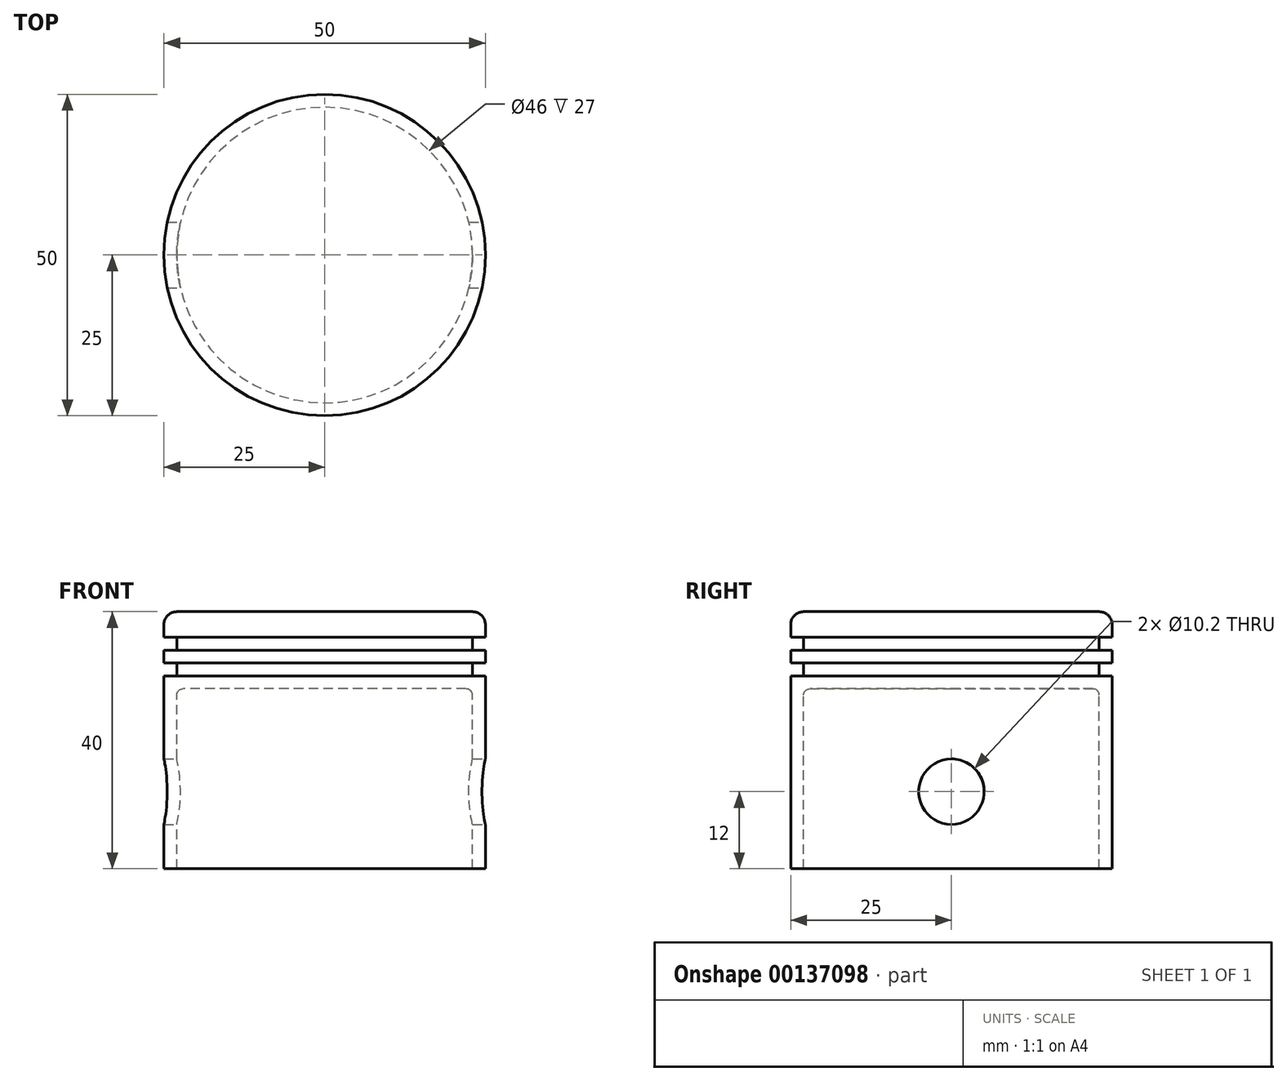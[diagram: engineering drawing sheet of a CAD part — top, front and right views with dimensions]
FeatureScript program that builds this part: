
annotation { "Feature Type Name" : "Feature", "Feature Type Description" : "" }
export const myFeature = defineFeature(function(context is Context, id is Id, definition is map)
    precondition{}
    {
        {
            var Q0;
            Q0=qCreatedBy(makeId("Right.planeOp"),FACE);
            var sketch = newSketch(context, id + "F0", { "sketchPlane" : qUnion([Q0])});
            skLineSegment(sketch, "E0.bottom", {"start": v(0, 20) * mm, "end": v(25, 20) * mm});
            skLineSegment(sketch, "E0.top", {"start": v(0, -20) * mm, "end": v(25, -20) * mm});
            skLineSegment(sketch, "E0.left", {"start": v(0, 20) * mm, "end": v(0, -20) * mm});
            skLineSegment(sketch, "E0.right", {"start": v(25, 20) * mm, "end": v(25, -20) * mm});
            skLineSegment(sketch, "E1.bottom", {"start": v(25, 16) * mm, "end": v(23, 16) * mm});
            skLineSegment(sketch, "E1.top", {"start": v(25, 14) * mm, "end": v(23, 14) * mm});
            skLineSegment(sketch, "E1.left", {"start": v(25, 16) * mm, "end": v(25, 14) * mm});
            skLineSegment(sketch, "E1.right", {"start": v(23, 16) * mm, "end": v(23, 14) * mm});
            skLineSegment(sketch, "E2.0.1.0", {"start": v(0, 16) * mm, "end": v(0, -24) * mm});
            skLineSegment(sketch, "E2.0.1.1", {"start": v(23, 12) * mm, "end": v(23, 10) * mm});
            skLineSegment(sketch, "E2.0.1.2", {"start": v(25, 10) * mm, "end": v(23, 10) * mm});
            skLineSegment(sketch, "E2.0.1.3", {"start": v(25, 12) * mm, "end": v(23, 12) * mm});
            skLineSegment(sketch, "E2.0.1.4", {"start": v(25, 12) * mm, "end": v(25, 10) * mm});
            skLineSegment(sketch, "E2.direction1", {"start": v(0, -20) * mm, "end": v(25, -20) * mm, "construction": true});
            skLineSegment(sketch, "E2.direction2", {"start": v(0, -20) * mm, "end": v(0, -24) * mm, "construction": true});
            skSolve(sketch);
        }
        {
            var Q0;
            {var subQ1=sQuery(id+"F0.wireOp",EDGE,"E0.bottom");Q0=makeQuery(id+"F0.imprint","IMPRINT",FACE,{"disambiguationData":[TD([[makeQuery(id+"F0.imprint","IMPRINT",EDGE,{"derivedFrom":subQ1}),-1.0]])]});}
            var Q1;
            Q1=sQuery(id+"F0.wireOp",EDGE,"E2.0.1.0");
            revolve(context, id + "F1", {"entities" : qUnion([Q0]), "axis" : qUnion([Q1]), "revolveType" : RevolveType.FULL});
        }
        {
            var Q0;
            Q0=makeQuery(id+"F1.opRevolve","SWEPT_EDGE",EDGE,{"disambiguationData":[OSD([sQuery(id+"F0.wireOp",EDGE,"E0.bottom"),sQuery(id+"F0.wireOp",EDGE,"E0.right")])]});
            fillet(context, id + "F2", {"entities" : qUnion([Q0]), "radius" : 2 * mm, "tangentPropagation" : true, "allowEdgeOverflow" : false});
        }
        {
            var Q0;
            Q0=qCreatedBy(makeId("Right.planeOp"),FACE);
            var sketch = newSketch(context, id + "F3", { "sketchPlane" : qUnion([Q0])});
            skLineSegment(sketch, "E3", {"start": v(0, -20) * mm, "end": v(0, 8) * mm});
            skLineSegment(sketch, "E4", {"start": v(0, 8) * mm, "end": v(22, 8) * mm});
            skLineSegment(sketch, "E5", {"start": v(23, 7) * mm, "end": v(23, -20) * mm});
            skLineSegment(sketch, "E6.0", {"start": v(-25, 10) * mm, "end": v(25, 10) * mm});
            skLineSegment(sketch, "E7.0", {"start": v(-25, 12) * mm, "end": v(25, 12) * mm});
            skLineSegment(sketch, "E7.1", {"start": v(-25, 14) * mm, "end": v(25, 14) * mm});
            skLineSegment(sketch, "E7.2", {"start": v(-25, 16) * mm, "end": v(25, 16) * mm});
            skLineSegment(sketch, "E7.3", {"start": v(25, 18) * mm, "end": v(-25, 18) * mm});
            skPoint(sketch, "E8.visualSharp", {"position": v(23, 8) * mm});
            skArc(sketch, "E8.filletArc", {"start": v(23, 7) * mm, "mid": v(22.7, 7.7) * mm, "end": v(22, 8) * mm});
            skLineSegment(sketch, "E9", {"start": v(0, -20) * mm, "end": v(23, -20) * mm});
            skPoint(sketch, "E10.orphan", {"position": v(-25, -20) * mm});
            skPoint(sketch, "E11.orphan", {"position": v(25, -20) * mm});
            skSolve(sketch);
        }
        {
            var Q0;
            Q0=makeQuery(id+"F3.imprint","IMPRINT",FACE,{"disambiguationData":[TD([[makeQuery(id+"F3.imprint","IMPRINT",EDGE,{"derivedFrom":sQuery(id+"F3.wireOp",EDGE,"E3")}),-1.0]])]});
            var Q1;
            Q1=sQuery(id+"F3.wireOp",EDGE,"E3");
            revolve(context, id + "F4", {"operationType" : NewBodyOperationType.REMOVE, "entities" : qUnion([Q0]), "axis" : qUnion([Q1]), "revolveType" : RevolveType.FULL, "oppositeDirection" : true});
        }
        {
            var Q0;
            Q0=qCreatedBy(makeId("Right.planeOp"),FACE);
            cPlane(context, id + "F5", {"entities" : qUnion([Q0]), "cplaneType" : CPlaneType.OFFSET, "offset" : 25 * mm, "width" : 150 * mm, "height" : 150 * mm});
        }
        {
            var Q0;
            Q0=qCreatedBy(id+"F5.planeOp",FACE);
            var sketch = newSketch(context, id + "F6", { "sketchPlane" : qUnion([Q0])});
            skPoint(sketch, "E12", {"position": v(0, -8) * mm});
            skSolve(sketch);
        }
        {
            var Q0;
            Q0=sQuery(id+"F6.wireOp",VERTEX,"E12");
            var Q1;
            Q1=makeQuery(id+"F1.opRevolve","SWEPT_BODY",BODY,{"disambiguationData":[OSD([sQuery(id+"F0.wireOp",EDGE,"E0.bottom"),sQuery(id+"F0.wireOp",EDGE,"E0.top"),sQuery(id+"F0.wireOp",EDGE,"E0.left"),sQuery(id+"F0.wireOp",EDGE,"E0.right"),sQuery(id+"F0.wireOp",EDGE,"E1.bottom"),sQuery(id+"F0.wireOp",EDGE,"E1.top"),sQuery(id+"F0.wireOp",EDGE,"E1.right"),sQuery(id+"F0.wireOp",EDGE,"E2.0.1.0"),sQuery(id+"F0.wireOp",EDGE,"E2.0.1.1"),sQuery(id+"F0.wireOp",EDGE,"E2.0.1.2"),sQuery(id+"F0.wireOp",EDGE,"E2.0.1.3")])]});
            hole(context, id + "F7", {"style" : HoleStyle.SIMPLE, "endStyle" : HoleEndStyle.THROUGH, "holeDiameter" : 10.2 * mm, "locations" : qUnion([Q0]), "scope" : qUnion([Q1]), "isTappedThrough" : true});
        }
    });
